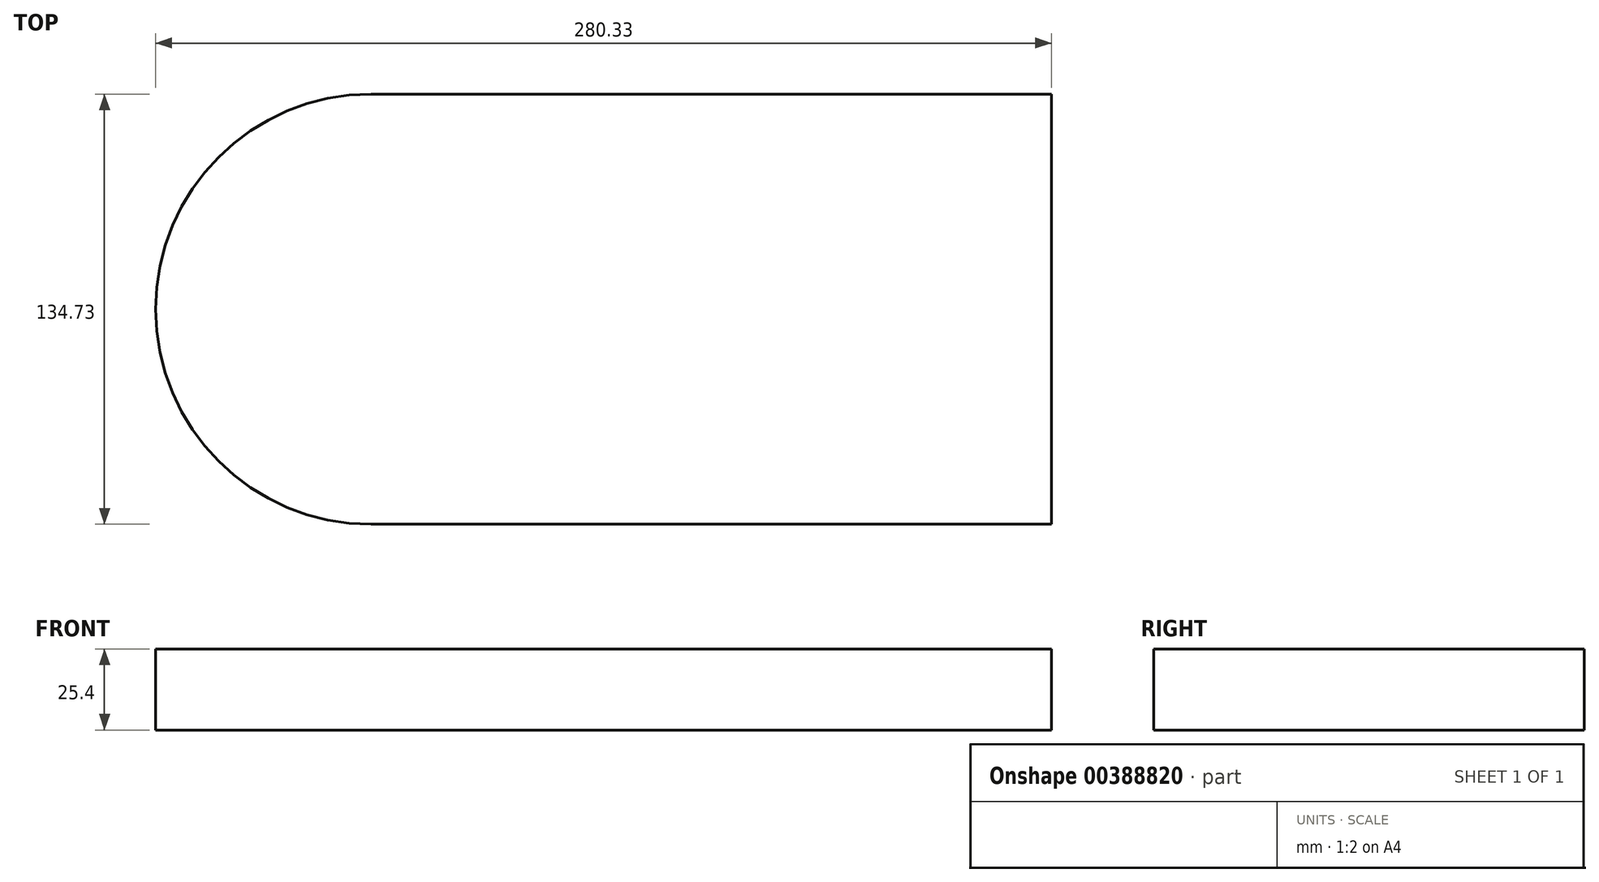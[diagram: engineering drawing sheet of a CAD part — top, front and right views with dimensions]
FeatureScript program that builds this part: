
annotation { "Feature Type Name" : "Feature", "Feature Type Description" : "" }
export const myFeature = defineFeature(function(context is Context, id is Id, definition is map)
    precondition{}
    {
        {
            var Q0;
            Q0=qCreatedBy(makeId("Top.planeOp"),FACE);
            var sketch = newSketch(context, id + "F0", { "sketchPlane" : qUnion([Q0])});
            skLineSegment(sketch, "E0.bottom", {"start": v(-8.93, -55.04) * mm, "end": v(-221.9, -55.04) * mm});
            skLineSegment(sketch, "E0.top", {"start": v(-8.93, 79.7) * mm, "end": v(-221.9, 79.7) * mm});
            skLineSegment(sketch, "E0.left", {"start": v(-8.93, -55.04) * mm, "end": v(-8.93, 79.7) * mm});
            skLineSegment(sketch, "E0.right", {"start": v(-221.9, -55.04) * mm, "end": v(-221.9, 79.7) * mm});
            skPoint(sketch, "E0.middle", {"position": v(-115.42, 12.33) * mm});
            skCircle(sketch, "E1", {"center": v(-221.9, 12.33) * mm, "radius": 67.37 * mm});
            skSolve(sketch);
        }
        {
            var Q0;
            Q0 = qSketchRegion(id + "F0", true);
            extrude(context, id + "F1", {"entities" : qUnion([Q0]), "depth" : 25.4 * mm});
        }
    });
